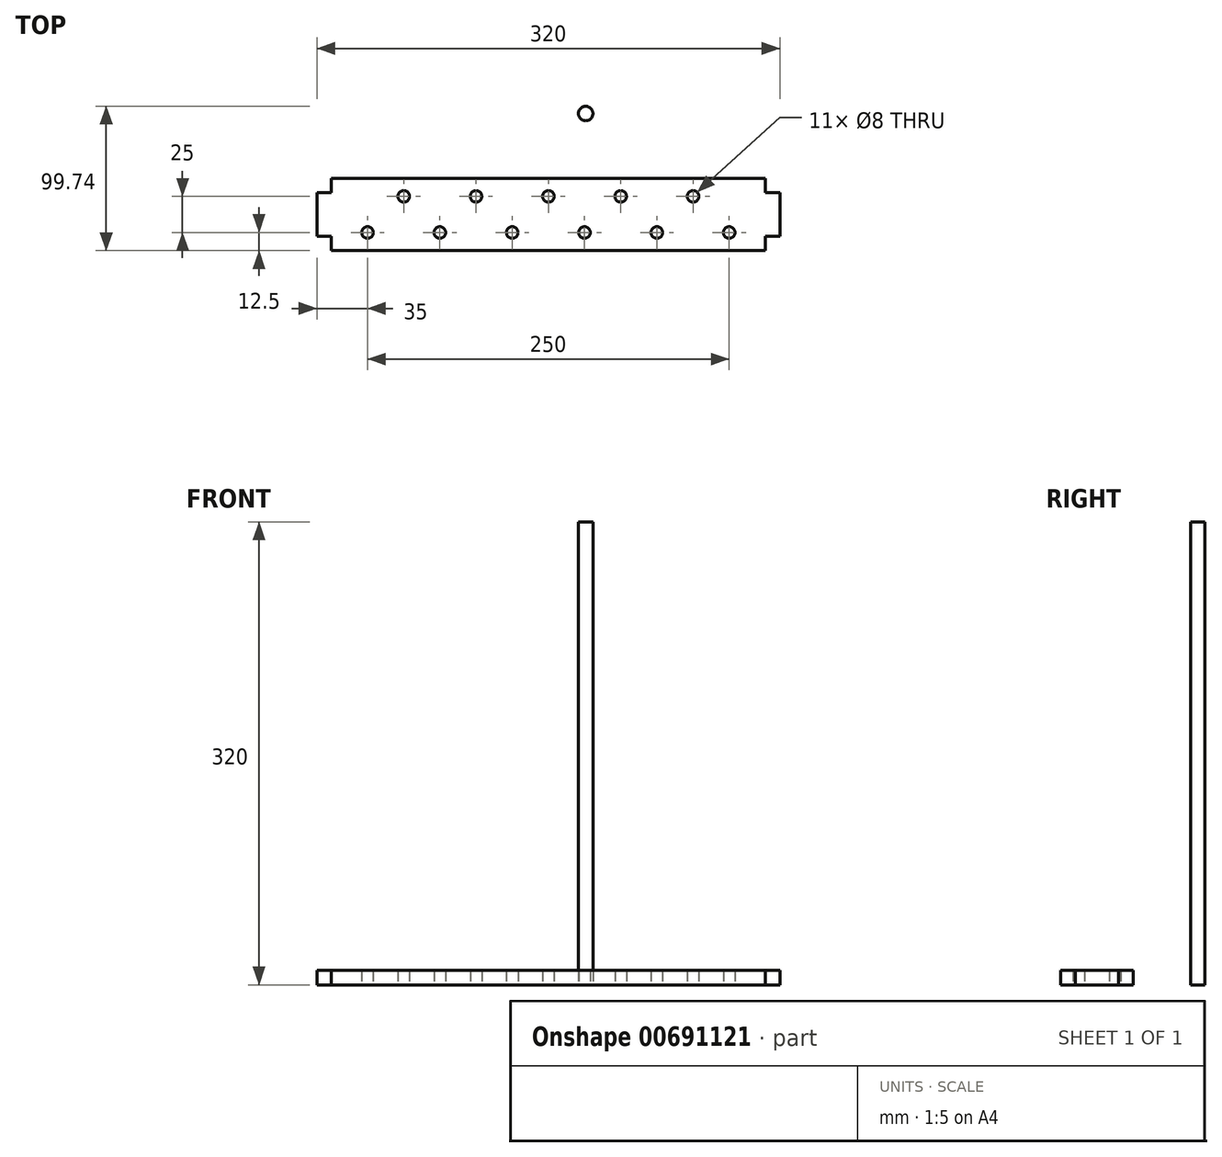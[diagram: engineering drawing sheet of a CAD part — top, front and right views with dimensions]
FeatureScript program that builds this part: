
annotation { "Feature Type Name" : "Feature", "Feature Type Description" : "" }
export const myFeature = defineFeature(function(context is Context, id is Id, definition is map)
    precondition{}
    {
        {
            var Q0;
            Q0=qCreatedBy(makeId("Top.planeOp"),FACE);
            var sketch = newSketch(context, id + "F0", { "sketchPlane" : qUnion([Q0])});
            skLineSegment(sketch, "E0.bottom", {"start": v(150, -25) * mm, "end": v(-150, -25) * mm});
            skLineSegment(sketch, "E0.top", {"start": v(150, 25) * mm, "end": v(-150, 25) * mm});
            skLineSegment(sketch, "E0.left", {"start": v(160, -15) * mm, "end": v(160, 15) * mm});
            skLineSegment(sketch, "E0.right", {"start": v(-160, -15) * mm, "end": v(-160, 15) * mm});
            skPoint(sketch, "E0.middle", {"position": v(0, 0) * mm});
            skLineSegment(sketch, "E1", {"start": v(-150, 25) * mm, "end": v(-150, -25) * mm});
            skLineSegment(sketch, "E2", {"start": v(150, 25) * mm, "end": v(150, -25) * mm});
            skCircle(sketch, "E3", {"center": v(-125, -12.5) * mm, "radius": 4 * mm});
            skCircle(sketch, "E4", {"center": v(-75, -12.5) * mm, "radius": 4 * mm});
            skCircle(sketch, "E5", {"center": v(-25, -12.5) * mm, "radius": 4 * mm});
            skCircle(sketch, "E6", {"center": v(25, -12.5) * mm, "radius": 4 * mm});
            skCircle(sketch, "E7", {"center": v(75, -12.5) * mm, "radius": 4 * mm});
            skCircle(sketch, "E8", {"center": v(-100, 12.5) * mm, "radius": 4 * mm});
            skCircle(sketch, "E9", {"center": v(125, -12.5) * mm, "radius": 4 * mm});
            skCircle(sketch, "E10", {"center": v(-50, 12.5) * mm, "radius": 4 * mm});
            skCircle(sketch, "E11", {"center": v(0, 12.5) * mm, "radius": 4 * mm});
            skCircle(sketch, "E12", {"center": v(50, 12.5) * mm, "radius": 4 * mm});
            skCircle(sketch, "E13", {"center": v(100, 12.5) * mm, "radius": 4 * mm});
            skLineSegment(sketch, "E14", {"start": v(150, 15) * mm, "end": v(160, 15) * mm});
            skLineSegment(sketch, "E15", {"start": v(150, -15) * mm, "end": v(160, -15) * mm});
            skLineSegment(sketch, "E16.MirrorCS", {"start": v(-150, 15) * mm, "end": v(-160, 15) * mm});
            skLineSegment(sketch, "E17.MirrorCS", {"start": v(-150, -15) * mm, "end": v(-160, -15) * mm});
            skLineSegment(sketch, "E18", {"start": v(150, 15) * mm, "end": v(150, 25) * mm});
            skLineSegment(sketch, "E19", {"start": v(150, -25) * mm, "end": v(150, -15) * mm});
            skLineSegment(sketch, "E20", {"start": v(-150, 25) * mm, "end": v(-150, 15) * mm});
            skPoint(sketch, "E21.orphan", {"position": v(160, 25) * mm});
            skPoint(sketch, "E22.orphan", {"position": v(160, -25) * mm});
            skPoint(sketch, "E23.orphan", {"position": v(-160, 25) * mm});
            skPoint(sketch, "E24.start.orphan", {"position": v(-160, -25) * mm});
            skSolve(sketch);
        }
        {
            var Q0;
            {var subQ4=sQuery(id+"F0.wireOp",EDGE,"E0.bottom");Q0=qUnion([makeQuery(id+"F0.imprint","IMPRINT",FACE,{"disambiguationData":[TD([[makeQuery(id+"F0.imprint","IMPRINT",EDGE,{"derivedFrom":sQuery(id+"F0.wireOp",EDGE,"E0.left")}),1.0]])]}),makeQuery(id+"F0.imprint","IMPRINT",FACE,{"disambiguationData":[TD([[makeQuery(id+"F0.imprint","IMPRINT",EDGE,{"derivedFrom":sQuery(id+"F0.wireOp",EDGE,"E0.right")}),-1.0]])]}),makeQuery(id+"F0.imprint","IMPRINT",FACE,{"disambiguationData":[TD([[makeQuery(id+"F0.imprint","IMPRINT",EDGE,{"derivedFrom":subQ4}),-1.0]])]})]);}
            extrude(context, id + "F1", {"entities" : qUnion([Q0]), "depth" : 10 * mm, "offsetDistance" : 25 * mm});
        }
        {
            var Q0;
            Q0=qCreatedBy(makeId("Top.planeOp"),FACE);
            var sketch = newSketch(context, id + "F2", { "sketchPlane" : qUnion([Q0])});
            skCircle(sketch, "E25", {"center": v(25.8, 69.74) * mm, "radius": 5 * mm});
            skSolve(sketch);
        }
        {
            var Q0;
            Q0=makeQuery(id+"F2.imprint","IMPRINT",FACE,{"disambiguationData":[TD([[makeQuery(id+"F2.imprint","IMPRINT",EDGE,{"derivedFrom":sQuery(id+"F2.wireOp",EDGE,"E25")}),1.0]])]});
            extrude(context, id + "F3", {"entities" : qUnion([Q0]), "depth" : 320 * mm, "offsetDistance" : 25 * mm});
        }
    });
